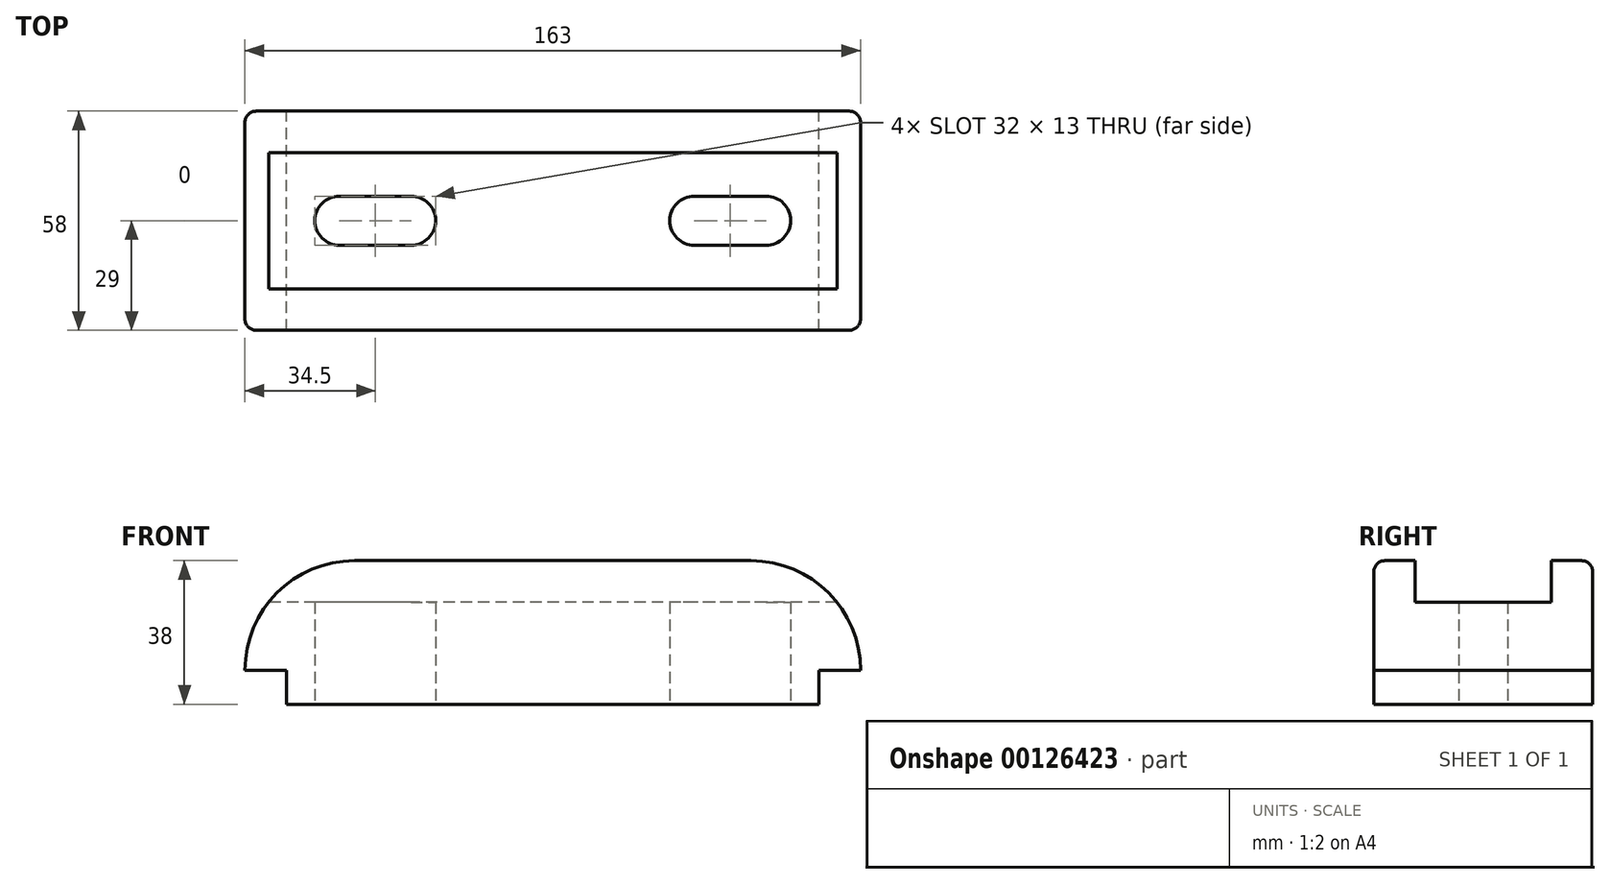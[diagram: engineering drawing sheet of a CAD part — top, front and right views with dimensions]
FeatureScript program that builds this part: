
annotation { "Feature Type Name" : "Feature", "Feature Type Description" : "" }
export const myFeature = defineFeature(function(context is Context, id is Id, definition is map)
    precondition{}
    {
        {
            var Q0;
            Q0=qCreatedBy(makeId("Front.planeOp"),FACE);
            var sketch = newSketch(context, id + "F0", { "sketchPlane" : qUnion([Q0])});
            skArc(sketch, "E0", {"start": v(29, 29) * mm, "mid": v(8.5, 20.5) * mm, "end": v(0, 0) * mm});
            skLineSegment(sketch, "E1", {"start": v(29, 29) * mm, "end": v(134, 29) * mm});
            skArc(sketch, "E2", {"start": v(163, 0) * mm, "mid": v(154.5, 20.5) * mm, "end": v(134, 29) * mm});
            skLineSegment(sketch, "E3", {"start": v(0, 0) * mm, "end": v(11, 0) * mm});
            skLineSegment(sketch, "E4", {"start": v(11, 0) * mm, "end": v(11, -9) * mm});
            skLineSegment(sketch, "E5", {"start": v(11, -9) * mm, "end": v(152, -9) * mm});
            skLineSegment(sketch, "E6", {"start": v(152, -9) * mm, "end": v(152, 0) * mm});
            skLineSegment(sketch, "E7", {"start": v(152, 0) * mm, "end": v(163, 0) * mm});
            skSolve(sketch);
        }
        {
            var Q0;
            Q0=makeQuery(id+"F0.imprint","IMPRINT",FACE,{"disambiguationData":[TD([[makeQuery(id+"F0.imprint","IMPRINT",EDGE,{"derivedFrom":sQuery(id+"F0.wireOp",EDGE,"E0")}),1.0]])]});
            extrude(context, id + "F1", {"entities" : qUnion([Q0]), "depth" : 58 * mm});
        }
        {
            var Q0;
            Q0=qCreatedBy(makeId("Right.planeOp"),FACE);
            var sketch = newSketch(context, id + "F2", { "sketchPlane" : qUnion([Q0])});
            skLineSegment(sketch, "E8", {"start": v(0, 0) * mm, "end": v(-29, 0) * mm, "construction": true});
            skLineSegment(sketch, "E9", {"start": v(-29, 0) * mm, "end": v(-29, 29) * mm, "construction": true});
            skLineSegment(sketch, "E10.bottom", {"start": v(-29, 29) * mm, "end": v(-47, 29) * mm});
            skLineSegment(sketch, "E10.top", {"start": v(-29, 18) * mm, "end": v(-47, 18) * mm});
            skLineSegment(sketch, "E10.left", {"start": v(-29, 29) * mm, "end": v(-29, 18) * mm});
            skLineSegment(sketch, "E10.right", {"start": v(-47, 29) * mm, "end": v(-47, 18) * mm});
            skPoint(sketch, "E11.oppositeSnap0", {"position": v(-38, 18) * mm});
            skLineSegment(sketch, "E11.bottom", {"start": v(-29, 29) * mm, "end": v(-11, 29) * mm});
            skLineSegment(sketch, "E11.top", {"start": v(-29, 18) * mm, "end": v(-11, 18) * mm});
            skLineSegment(sketch, "E11.right", {"start": v(-11, 29) * mm, "end": v(-11, 18) * mm});
            skLineSegment(sketch, "E12", {"start": v(-47, 29) * mm, "end": v(-11, 29) * mm, "construction": true});
            skLineSegment(sketch, "E13", {"start": v(-47, 29) * mm, "end": v(-11, 29) * mm});
            skSolve(sketch);
        }
        {
            var Q0;
            Q0 = qSketchRegion(id + "F2", true);
            extrude(context, id + "F3", {"entities" : qUnion([Q0]), "operationType" : NewBodyOperationType.REMOVE, "endBound" : BoundingType.THROUGH_ALL, "depth" : 25 * mm});
        }
        {
            var Q0;
            Q0=makeQuery(id+"F1.opExtrude","CAP_EDGE",EDGE,{"disambiguationData":[OSD([sQuery(id+"F0.wireOp",EDGE,"E0")])],"isStart":false});
            var Q1;
            Q1=makeQuery(id+"F1.opExtrude","CAP_EDGE",EDGE,{"disambiguationData":[OSD([sQuery(id+"F0.wireOp",EDGE,"E1")])],"isStart":false});
            var Q2;
            Q2=makeQuery(id+"F1.opExtrude","CAP_EDGE",EDGE,{"disambiguationData":[OSD([sQuery(id+"F0.wireOp",EDGE,"E2")])],"isStart":false});
            var Q3;
            Q3=makeQuery(id+"F1.opExtrude","CAP_EDGE",EDGE,{"disambiguationData":[OSD([sQuery(id+"F0.wireOp",EDGE,"E0")])],"isStart":true});
            fillet(context, id + "F4", {"entities" : qUnion([Q0, Q1, Q2, Q3]), "radius" : 3 * mm, "tangentPropagation" : true, "allowEdgeOverflow" : false});
        }
        {
            var Q0;
            Q0=makeQuery(id+"F1.opExtrude","SWEPT_FACE",FACE,{"disambiguationData":[OSD([sQuery(id+"F0.wireOp",EDGE,"E5")])]});
            var sketch = newSketch(context, id + "F5", { "sketchPlane" : qUnion([Q0])});
            skLineSegment(sketch, "E14", {"start": v(152, 58) * mm, "end": v(152, 29) * mm, "construction": true});
            skLineSegment(sketch, "E15", {"start": v(11, 29) * mm, "end": v(152, 29) * mm, "construction": true});
            skCircle(sketch, "E16", {"center": v(138, 29) * mm, "radius": 6.5 * mm});
            skCircle(sketch, "E17", {"center": v(119, 29) * mm, "radius": 6.5 * mm});
            skCircle(sketch, "E18", {"center": v(25, 29) * mm, "radius": 6.5 * mm});
            skCircle(sketch, "E19", {"center": v(44, 29) * mm, "radius": 6.5 * mm});
            skLineSegment(sketch, "E20", {"start": v(138, 22.5) * mm, "end": v(119, 22.5) * mm});
            skLineSegment(sketch, "E21", {"start": v(119, 35.5) * mm, "end": v(138, 35.5) * mm});
            skLineSegment(sketch, "E22", {"start": v(44, 22.5) * mm, "end": v(25, 22.5) * mm});
            skLineSegment(sketch, "E23", {"start": v(44, 35.5) * mm, "end": v(25, 35.5) * mm});
            skSolve(sketch);
        }
        {
            var Q0;
            Q0 = qSketchRegion(id + "F5", true);
            extrude(context, id + "F6", {"entities" : qUnion([Q0]), "operationType" : NewBodyOperationType.REMOVE, "endBound" : BoundingType.THROUGH_ALL, "oppositeDirection" : true, "depth" : 25 * mm});
        }
    });
